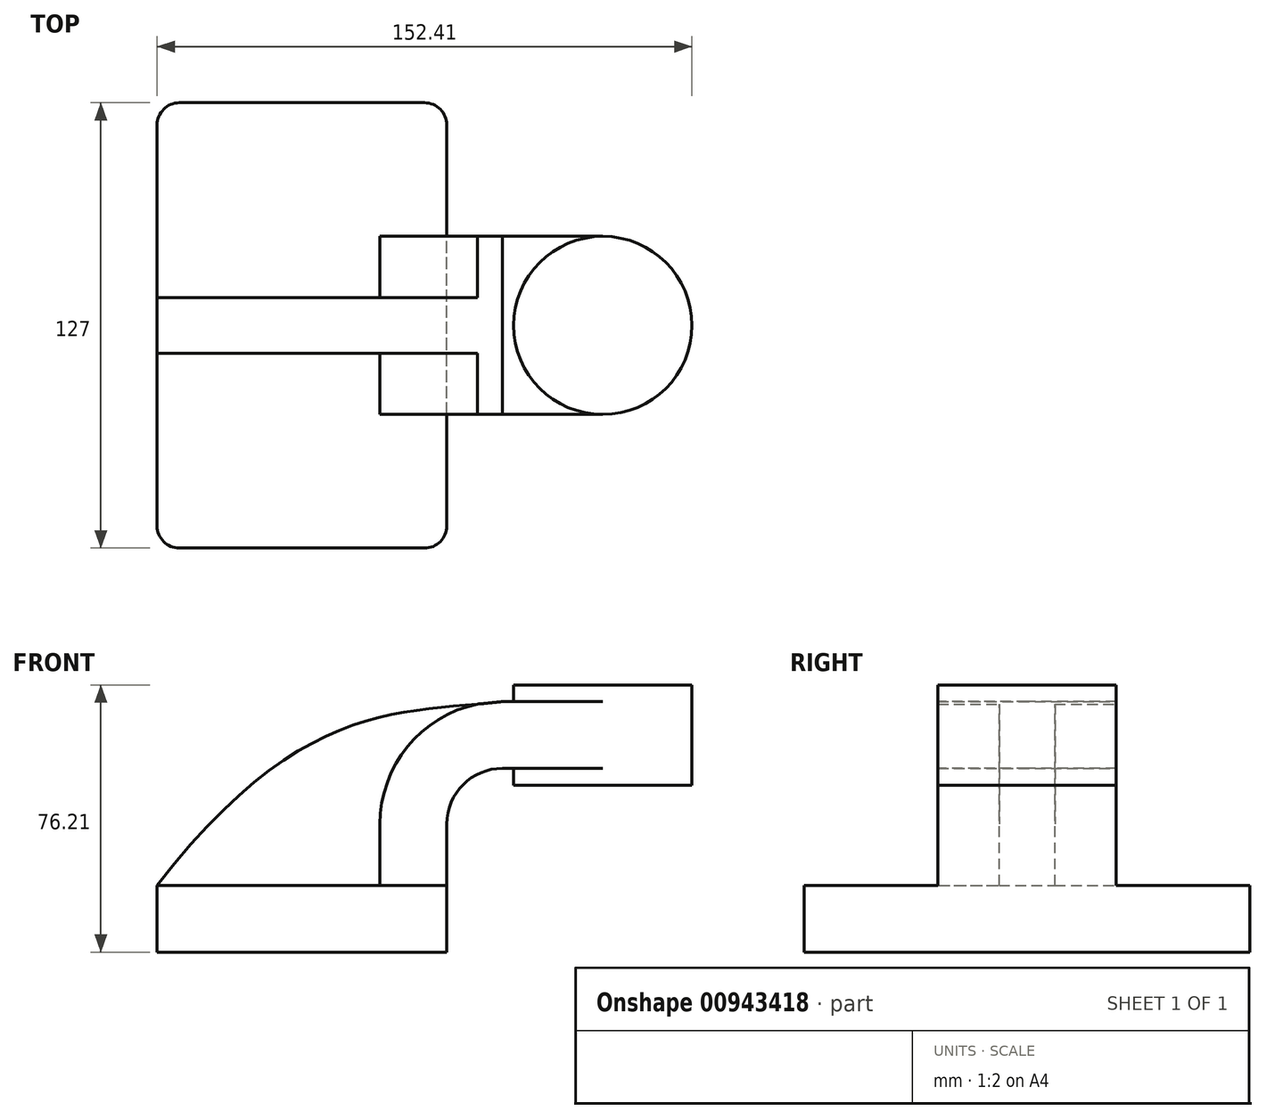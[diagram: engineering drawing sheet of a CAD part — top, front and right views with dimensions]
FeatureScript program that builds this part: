
annotation { "Feature Type Name" : "Feature", "Feature Type Description" : "" }
export const myFeature = defineFeature(function(context is Context, id is Id, definition is map)
    precondition{}
    {
        {
            var Q0;
            Q0=qCreatedBy(makeId("Front.planeOp"),FACE);
            var sketch = newSketch(context, id + "F0", { "sketchPlane" : qUnion([Q0])});
            skLineSegment(sketch, "E0.bottom", {"start": v(-41.28, -9.53) * mm, "end": v(41.28, -9.53) * mm});
            skLineSegment(sketch, "E0.top", {"start": v(-41.28, 9.53) * mm, "end": v(41.28, 9.53) * mm});
            skLineSegment(sketch, "E0.left", {"start": v(-41.28, -9.53) * mm, "end": v(-41.28, 9.53) * mm});
            skLineSegment(sketch, "E0.right", {"start": v(41.28, -9.53) * mm, "end": v(41.28, 9.53) * mm});
            skPoint(sketch, "E0.middle", {"position": v(0, 0) * mm});
            skLineSegment(sketch, "E1.bottom", {"start": v(60.32, 38.1) * mm, "end": v(111.12, 38.1) * mm});
            skLineSegment(sketch, "E1.top", {"start": v(60.32, 66.67) * mm, "end": v(111.12, 66.67) * mm});
            skLineSegment(sketch, "E1.left", {"start": v(60.33, 38.1) * mm, "end": v(60.32, 66.68) * mm});
            skLineSegment(sketch, "E1.right", {"start": v(111.12, 38.1) * mm, "end": v(111.12, 66.68) * mm});
            skPoint(sketch, "E1.middle", {"position": v(85.72, 52.39) * mm});
            skLineSegment(sketch, "E2", {"start": v(41.28, 9.53) * mm, "end": v(41.28, 27) * mm});
            skArc(sketch, "E3", {"start": v(57.15, 42.88) * mm, "mid": v(45.92, 38.23) * mm, "end": v(41.27, 27) * mm});
            skLineSegment(sketch, "E4", {"start": v(57.15, 42.88) * mm, "end": v(85.72, 42.88) * mm});
            skLineSegment(sketch, "E5.0", {"start": v(57.15, 61.93) * mm, "end": v(85.72, 61.93) * mm});
            skArc(sketch, "E5.1", {"start": v(57.15, 61.93) * mm, "mid": v(32.45, 51.7) * mm, "end": v(22.23, 27) * mm});
            skLineSegment(sketch, "E5.2", {"start": v(22.22, 9.53) * mm, "end": v(22.22, 27) * mm});
            skLineSegment(sketch, "E6", {"start": v(85.72, 38.1) * mm, "end": v(85.72, 66.67) * mm});
            skFitSpline(sketch, "E7", {"points": [v(-41.28, 9.53) * mm, v(57.15, 61.93) * mm], "startDerivative": vector(123.83, 160.58) * mm, "endDerivative": vector(85.9, 10.35) * mm});
            skSolve(sketch);
        }
        {
            var Q0;
            Q0=makeQuery(id+"F0.imprint","IMPRINT",FACE,{"disambiguationData":[TD([[makeQuery(id+"F0.imprint","IMPRINT",EDGE,{"derivedFrom":sQuery(id+"F0.wireOp",EDGE,"E0.bottom")}),1.0]])]});
            extrude(context, id + "F1", {"entities" : qUnion([Q0]), "endBound" : BoundingType.SYMMETRIC, "depth" : 127 * mm, "offsetDistance" : 25.4 * mm});
        }
        {
            var Q0;
            {var subQ0=sQuery(id+"F0.wireOp",EDGE,"E4");var subQ1=sQuery(id+"F0.wireOp",EDGE,"E1.left");var subQ2=makeQuery(id+"F0.imprint","INTERSECT",VERTEX,{"derivedFrom":[subQ1,subQ0]});Q0=makeQuery(id+"F0.imprint","IMPRINT",FACE,{"disambiguationData":[TD([[makeQuery(id+"F0.imprint","IMPRINT",EDGE,{"disambiguationData":[TD([[subQ2,-1.0]])],"derivedFrom":subQ1}),-1.0]])]});}
            var Q1;
            {var subQ1=sQuery(id+"F0.wireOp",EDGE,"E2");Q1=makeQuery(id+"F0.imprint","IMPRINT",FACE,{"disambiguationData":[TD([[makeQuery(id+"F0.imprint","IMPRINT",EDGE,{"derivedFrom":subQ1}),1.0]])]});}
            extrude(context, id + "F2", {"entities" : qUnion([Q0, Q1]), "operationType" : NewBodyOperationType.ADD, "endBound" : BoundingType.SYMMETRIC, "depth" : 50.8 * mm, "offsetDistance" : 25.4 * mm});
        }
        {
            var Q0;
            {var subQ3=sQuery(id+"F0.wireOp",EDGE,"E5.2");Q0=makeQuery(id+"F0.imprint","IMPRINT",FACE,{"disambiguationData":[TD([[makeQuery(id+"F0.imprint","IMPRINT",EDGE,{"derivedFrom":subQ3}),1.0]])]});}
            extrude(context, id + "F3", {"entities" : qUnion([Q0]), "operationType" : NewBodyOperationType.ADD, "endBound" : BoundingType.SYMMETRIC, "depth" : 15.88 * mm, "offsetDistance" : 25.4 * mm});
        }
        {
            var Q0;
            {var subQ4=sQuery(id+"F0.wireOp",EDGE,"E1.right");Q0=makeQuery(id+"F0.imprint","IMPRINT",FACE,{"disambiguationData":[TD([[makeQuery(id+"F0.imprint","IMPRINT",EDGE,{"derivedFrom":subQ4}),1.0]])]});}
            var Q1;
            Q1=sQuery(id+"F0.wireOp",EDGE,"E6");
            revolve(context, id + "F4", {"operationType" : NewBodyOperationType.ADD, "surfaceOperationType" : NewSurfaceOperationType.NEW, "entities" : qUnion([Q0]), "axis" : qUnion([Q1]), "revolveType" : RevolveType.FULL});
        }
        {
            var Q0;
            Q0=makeQuery(id+"F1.opExtrude","CAP_EDGE",EDGE,{"disambiguationData":[OSD([sQuery(id+"F0.wireOp",EDGE,"E0.left")])],"isStart":false});
            var Q1;
            Q1=makeQuery(id+"F1.opExtrude","CAP_EDGE",EDGE,{"disambiguationData":[OSD([sQuery(id+"F0.wireOp",EDGE,"E0.right")])],"isStart":false});
            var Q2;
            Q2=makeQuery(id+"F1.opExtrude","CAP_EDGE",EDGE,{"disambiguationData":[OSD([sQuery(id+"F0.wireOp",EDGE,"E0.right")])],"isStart":true});
            var Q3;
            Q3=makeQuery(id+"F1.opExtrude","CAP_EDGE",EDGE,{"disambiguationData":[OSD([sQuery(id+"F0.wireOp",EDGE,"E0.left")])],"isStart":true});
            fillet(context, id + "F5", {"entities" : qUnion([Q0, Q1, Q2, Q3]), "radius" : 6.35 * mm, "tangentPropagation" : true, "allowEdgeOverflow" : false});
        }
    });
